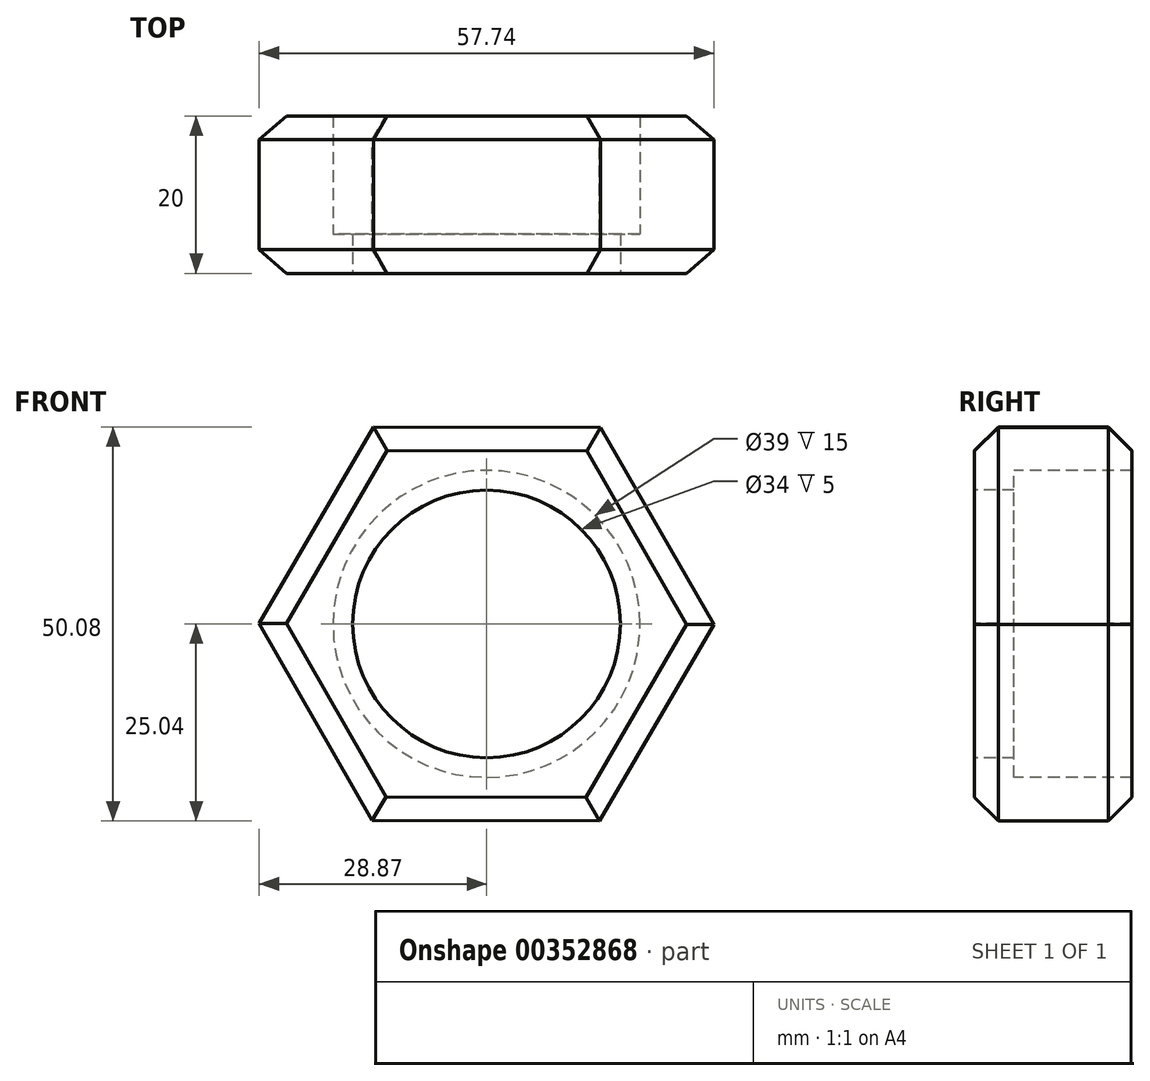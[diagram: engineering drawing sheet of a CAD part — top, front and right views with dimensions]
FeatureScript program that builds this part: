
annotation { "Feature Type Name" : "Feature", "Feature Type Description" : "" }
export const myFeature = defineFeature(function(context is Context, id is Id, definition is map)
    precondition{}
    {
        {
            var Q0;
            Q0=qCreatedBy(makeId("Front.planeOp"),FACE);
            var sketch = newSketch(context, id + "F0", { "sketchPlane" : qUnion([Q0])});
            skCircle(sketch, "E0.cCircle", {"center": v(0, 0) * mm, "radius": 25 * mm, "construction": true});
            skLineSegment(sketch, "E0.0", {"start": v(28.87, -0.09) * mm, "end": v(14.36, -25.04) * mm});
            skLineSegment(sketch, "E0.1", {"start": v(14.36, -25.04) * mm, "end": v(-14.51, -24.96) * mm});
            skLineSegment(sketch, "E0.2", {"start": v(-14.51, -24.96) * mm, "end": v(-28.87, 0.09) * mm});
            skLineSegment(sketch, "E0.3", {"start": v(-28.87, 0.09) * mm, "end": v(-14.36, 25.04) * mm});
            skLineSegment(sketch, "E0.4", {"start": v(-14.36, 25.04) * mm, "end": v(14.51, 24.96) * mm});
            skLineSegment(sketch, "E0.5", {"start": v(14.51, 24.96) * mm, "end": v(28.87, -0.09) * mm});
            skPoint(sketch, "E0.0.midPoint", {"position": v(21.61, -12.57) * mm});
            skSolve(sketch);
        }
        {
            var Q0;
            Q0 = qSketchRegion(id + "F0", true);
            extrude(context, id + "F1", {"entities" : qUnion([Q0]), "depth" : 20 * mm});
        }
        {
            var Q0;
            Q0=makeQuery(id+"F1.opExtrude","CAP_FACE",FACE,{"disambiguationData":[OSD([sQuery(id+"F0.wireOp",EDGE,"E0.0"),sQuery(id+"F0.wireOp",EDGE,"E0.1"),sQuery(id+"F0.wireOp",EDGE,"E0.2"),sQuery(id+"F0.wireOp",EDGE,"E0.3"),sQuery(id+"F0.wireOp",EDGE,"E0.4"),sQuery(id+"F0.wireOp",EDGE,"E0.5")])],"isStart":false});
            var sketch = newSketch(context, id + "F2", { "sketchPlane" : qUnion([Q0])});
            skCircle(sketch, "E1", {"center": v(0, 0) * mm, "radius": 19.5 * mm});
            skSolve(sketch);
        }
        {
            var Q0;
            Q0=sQuery(id+"F2.wireOp",VERTEX,"E1.center");
            var Q1;
            Q1=makeQuery(id+"F1.opExtrude","SWEPT_BODY",BODY,{"disambiguationData":[OSD([sQuery(id+"F0.wireOp",EDGE,"E0.0"),sQuery(id+"F0.wireOp",EDGE,"E0.1"),sQuery(id+"F0.wireOp",EDGE,"E0.2"),sQuery(id+"F0.wireOp",EDGE,"E0.3"),sQuery(id+"F0.wireOp",EDGE,"E0.4"),sQuery(id+"F0.wireOp",EDGE,"E0.5")])]});
            hole(context, id + "F3", {"style" : HoleStyle.SIMPLE, "endStyle" : HoleEndStyle.THROUGH, "holeDiameter" : 39 * mm, "isTappedThrough" : true, "tappedDepth" : 12 * mm, "tapClearance" : 3, "locations" : qUnion([Q0]), "scope" : qUnion([Q1])});
        }
        {
            var Q0;
            Q0=makeQuery(id+"F1.opExtrude","CAP_EDGE",EDGE,{"disambiguationData":[OSD([sQuery(id+"F0.wireOp",EDGE,"E0.3")])],"isStart":false});
            var Q1;
            Q1=makeQuery(id+"F1.opExtrude","CAP_EDGE",EDGE,{"disambiguationData":[OSD([sQuery(id+"F0.wireOp",EDGE,"E0.4")])],"isStart":false});
            var Q2;
            Q2=makeQuery(id+"F1.opExtrude","CAP_EDGE",EDGE,{"disambiguationData":[OSD([sQuery(id+"F0.wireOp",EDGE,"E0.5")])],"isStart":false});
            var Q3;
            Q3=makeQuery(id+"F1.opExtrude","CAP_EDGE",EDGE,{"disambiguationData":[OSD([sQuery(id+"F0.wireOp",EDGE,"E0.0")])],"isStart":false});
            var Q4;
            Q4=makeQuery(id+"F1.opExtrude","CAP_EDGE",EDGE,{"disambiguationData":[OSD([sQuery(id+"F0.wireOp",EDGE,"E0.1")])],"isStart":false});
            var Q5;
            Q5=makeQuery(id+"F1.opExtrude","CAP_EDGE",EDGE,{"disambiguationData":[OSD([sQuery(id+"F0.wireOp",EDGE,"E0.2")])],"isStart":false});
            var Q6;
            Q6=makeQuery(id+"F1.opExtrude","CAP_EDGE",EDGE,{"disambiguationData":[OSD([sQuery(id+"F0.wireOp",EDGE,"E0.5")])],"isStart":true});
            var Q7;
            Q7=makeQuery(id+"F1.opExtrude","CAP_EDGE",EDGE,{"disambiguationData":[OSD([sQuery(id+"F0.wireOp",EDGE,"E0.0")])],"isStart":true});
            var Q8;
            Q8=makeQuery(id+"F1.opExtrude","CAP_EDGE",EDGE,{"disambiguationData":[OSD([sQuery(id+"F0.wireOp",EDGE,"E0.1")])],"isStart":true});
            var Q9;
            Q9=makeQuery(id+"F1.opExtrude","CAP_EDGE",EDGE,{"disambiguationData":[OSD([sQuery(id+"F0.wireOp",EDGE,"E0.2")])],"isStart":true});
            var Q10;
            Q10=makeQuery(id+"F1.opExtrude","CAP_EDGE",EDGE,{"disambiguationData":[OSD([sQuery(id+"F0.wireOp",EDGE,"E0.3")])],"isStart":true});
            var Q11;
            Q11=makeQuery(id+"F1.opExtrude","CAP_EDGE",EDGE,{"disambiguationData":[OSD([sQuery(id+"F0.wireOp",EDGE,"E0.4")])],"isStart":true});
            chamfer(context, id + "F4", {"entities" : qUnion([Q0, Q1, Q2, Q3, Q4, Q5, Q6, Q7, Q8, Q9, Q10, Q11]), "width" : 3 * mm, "tangentPropagation" : true});
        }
        {
            var Q0;
            Q0=makeQuery(id+"F1.opExtrude","CAP_FACE",FACE,{"disambiguationData":[OSD([sQuery(id+"F0.wireOp",EDGE,"E0.0"),sQuery(id+"F0.wireOp",EDGE,"E0.1"),sQuery(id+"F0.wireOp",EDGE,"E0.2"),sQuery(id+"F0.wireOp",EDGE,"E0.3"),sQuery(id+"F0.wireOp",EDGE,"E0.4"),sQuery(id+"F0.wireOp",EDGE,"E0.5")])],"isStart":false});
            var sketch = newSketch(context, id + "F5", { "sketchPlane" : qUnion([Q0])});
            skCircle(sketch, "E2", {"center": v(0, 0) * mm, "radius": 19.5 * mm});
            skCircle(sketch, "E3", {"center": v(0, 0) * mm, "radius": 17 * mm});
            skSolve(sketch);
        }
        {
            var Q0;
            Q0=makeQuery(id+"F5.imprint","IMPRINT",FACE,{"disambiguationData":[TD([[makeQuery(id+"F5.imprint","IMPRINT",EDGE,{"derivedFrom":sQuery(id+"F5.wireOp",EDGE,"E2")}),1.0]])]});
            extrude(context, id + "F6", {"entities" : qUnion([Q0]), "operationType" : NewBodyOperationType.ADD, "oppositeDirection" : true, "depth" : 5 * mm});
        }
    });
